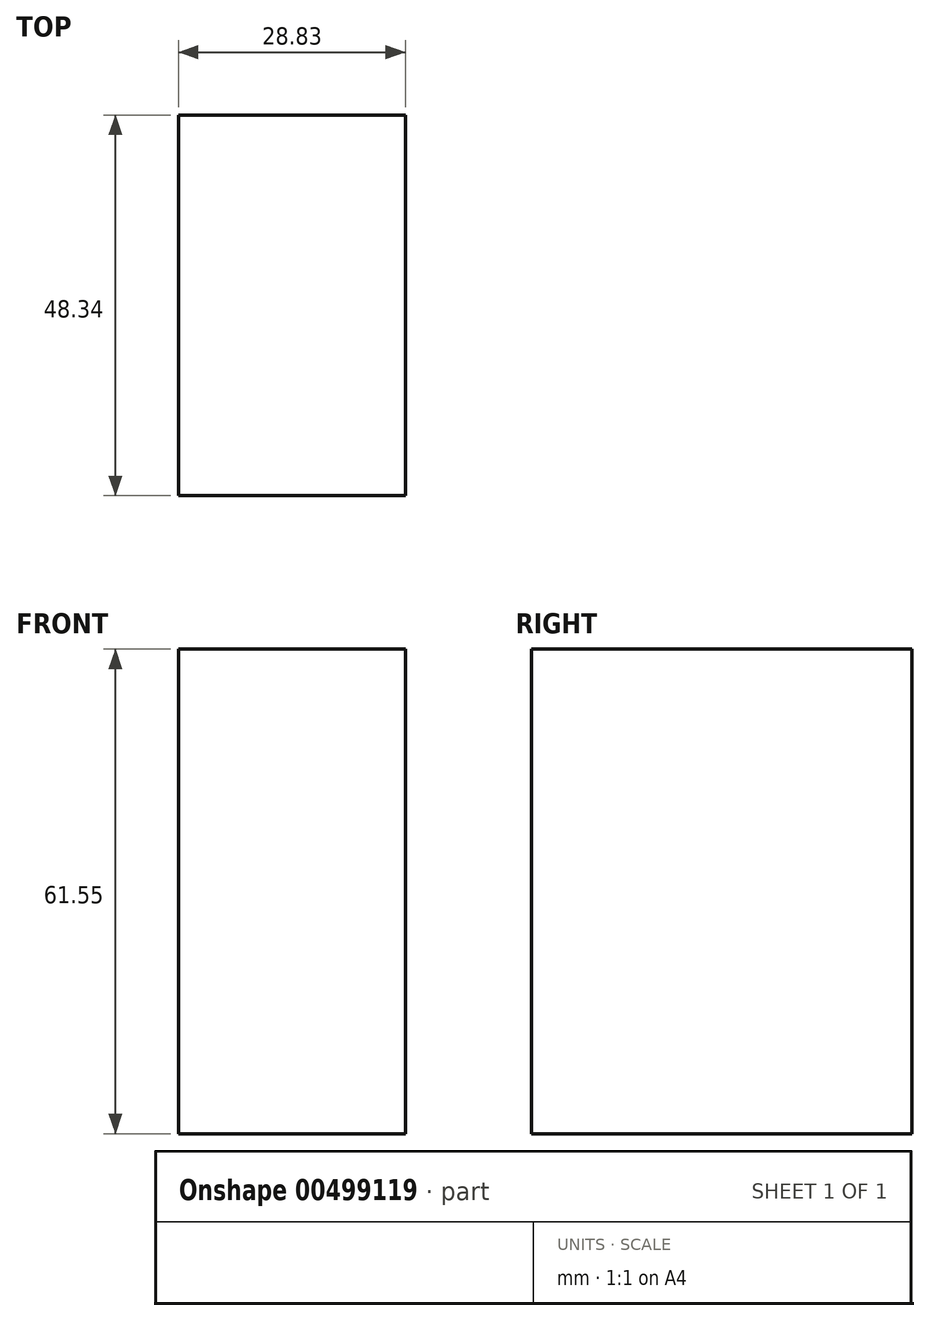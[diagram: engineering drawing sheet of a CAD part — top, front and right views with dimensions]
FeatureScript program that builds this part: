
annotation { "Feature Type Name" : "Feature", "Feature Type Description" : "" }
export const myFeature = defineFeature(function(context is Context, id is Id, definition is map)
    precondition{}
    {
        {
            var Q0;
            Q0=qCreatedBy(makeId("Top.planeOp"),FACE);
            var sketch = newSketch(context, id + "F0", { "sketchPlane" : qUnion([Q0])});
            skLineSegment(sketch, "E0.bottom", {"start": v(28.83, 0) * mm, "end": v(0, 0) * mm});
            skLineSegment(sketch, "E0.top", {"start": v(28.83, -48.34) * mm, "end": v(0, -48.34) * mm});
            skLineSegment(sketch, "E0.left", {"start": v(28.83, 0) * mm, "end": v(28.83, -48.34) * mm});
            skLineSegment(sketch, "E0.right", {"start": v(0, 0) * mm, "end": v(0, -48.34) * mm});
            skSolve(sketch);
        }
        {
            var Q0;
            Q0=makeQuery(id+"F0.imprint","IMPRINT",FACE,{"disambiguationData":[TD([[makeQuery(id+"F0.imprint","IMPRINT",EDGE,{"derivedFrom":sQuery(id+"F0.wireOp",EDGE,"E0.bottom")}),1.0]])]});
            extrude(context, id + "F1", {"entities" : qUnion([Q0]), "depth" : 61.55 * mm});
        }
    });
